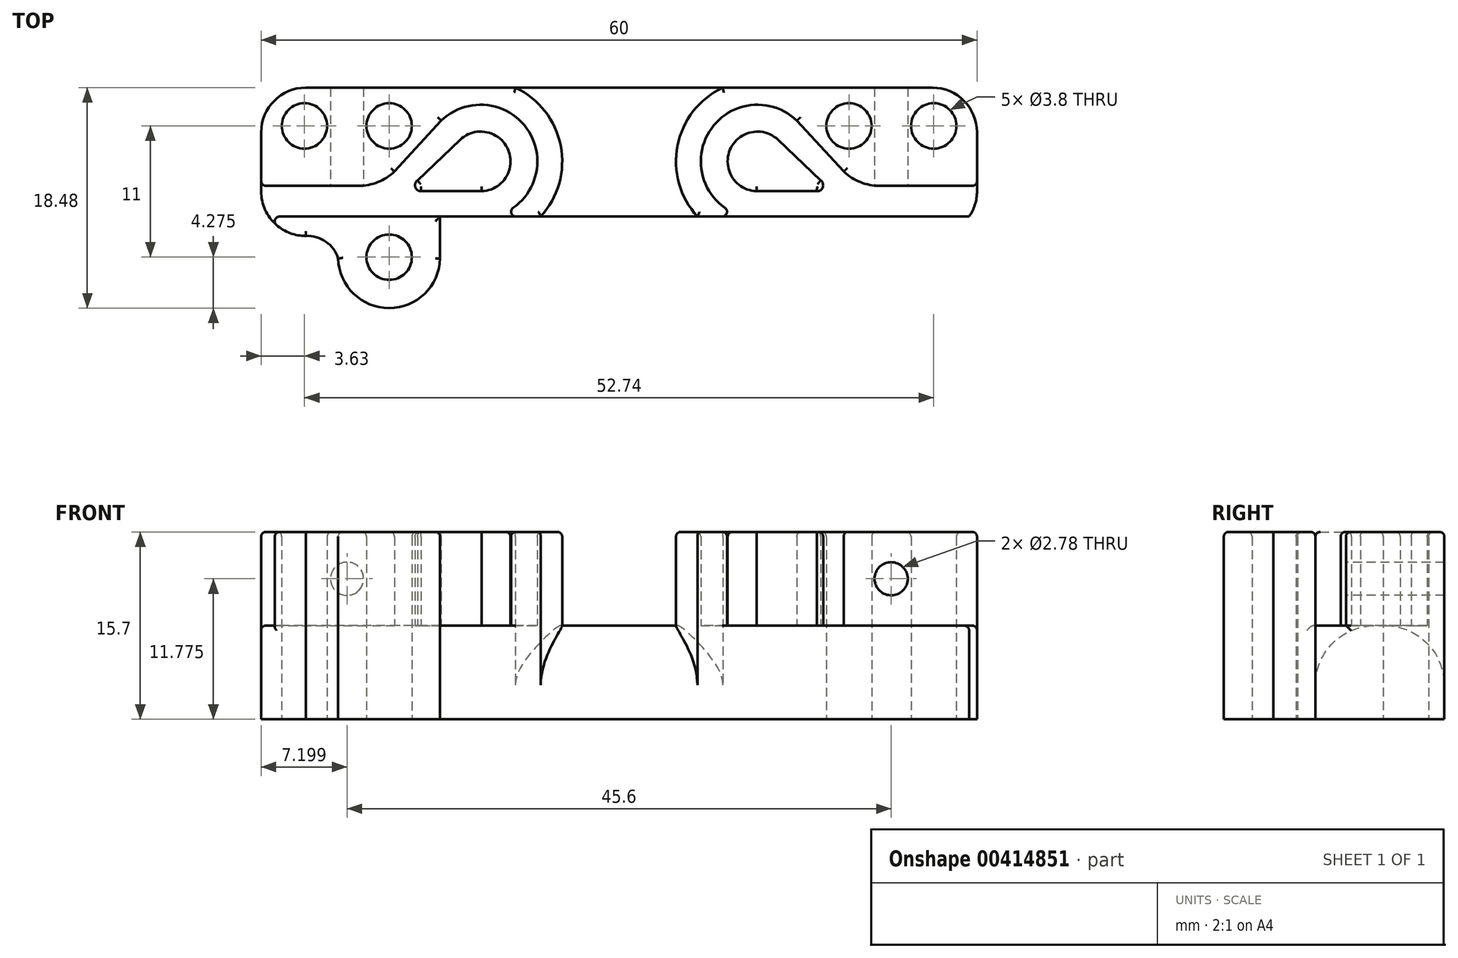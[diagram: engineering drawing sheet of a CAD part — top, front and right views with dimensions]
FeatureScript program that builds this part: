
annotation { "Feature Type Name" : "Feature", "Feature Type Description" : "" }
export const myFeature = defineFeature(function(context is Context, id is Id, definition is map)
    precondition{}
    {
        {
            var Q0;
            Q0=qCreatedBy(makeId("Top.planeOp"),FACE);
            cPlane(context, id + "F0", {"entities" : qUnion([Q0]), "cplaneType" : CPlaneType.OFFSET, "offset" : 7.85 * mm, "oppositeDirection" : true, "width" : 150 * mm, "height" : 150 * mm});
        }
        {
            var Q0;
            Q0=qCreatedBy(id+"F0.planeOp",FACE);
            var sketch = newSketch(context, id + "F1", { "sketchPlane" : qUnion([Q0])});
            skLineSegment(sketch, "E0.left", {"start": v(-30, 9) * mm, "end": v(-30, -9) * mm, "construction": true});
            skLineSegment(sketch, "E0.right", {"start": v(30, 9) * mm, "end": v(30, -9) * mm, "construction": true});
            skPoint(sketch, "E0.middle", {"position": v(0, 0) * mm});
            skLineSegment(sketch, "E1", {"start": v(0, 10.81) * mm, "end": v(0, -11.68) * mm, "construction": true});
            skCircle(sketch, "E2", {"center": v(-16.6, 0.82) * mm, "radius": 0.5 * mm, "construction": true});
            skLineSegment(sketch, "E3", {"start": v(-16.9, 1.23) * mm, "end": v(-13.32, 4.63) * mm});
            skLineSegment(sketch, "E4", {"start": v(-16.59, 0.32) * mm, "end": v(-11.53, 0.32) * mm});
            skArc(sketch, "E5", {"start": v(-13.32, 4.63) * mm, "mid": v(-9.3, 3.78) * mm, "end": v(-11.53, 0.32) * mm});
            skArc(sketch, "E6", {"start": v(-16.9, 1.23) * mm, "mid": v(-17.08, 0.66) * mm, "end": v(-16.59, 0.32) * mm});
            skLineSegment(sketch, "E7", {"start": v(-14.9, 6.23) * mm, "end": v(-18.83, 1.97) * mm});
            skLineSegment(sketch, "E8", {"start": v(-30, 0.77) * mm, "end": v(-21.86, 0.77) * mm});
            skArc(sketch, "E9", {"start": v(-21.86, 0.77) * mm, "mid": v(-20.23, 1.08) * mm, "end": v(-18.83, 1.97) * mm});
            skArc(sketch, "E10", {"start": v(-10.5, -1.8) * mm, "mid": v(-7.44, 5.1) * mm, "end": v(-14.9, 6.23) * mm});
            skCircle(sketch, "E11", {"center": v(-19.27, -5.2) * mm, "radius": 1.9 * mm});
            skCircle(sketch, "E12", {"center": v(-19.27, 5.8) * mm, "radius": 1.9 * mm});
            skCircle(sketch, "E13", {"center": v(-26.37, 5.8) * mm, "radius": 1.9 * mm});
            skLineSegment(sketch, "E14", {"start": v(-15, -1.8) * mm, "end": v(-15, -5.32) * mm});
            skArc(sketch, "E15", {"start": v(-15, -5.32) * mm, "mid": v(-19.27, -9.48) * mm, "end": v(-23.54, -5.32) * mm});
            skArc(sketch, "E16", {"start": v(-30, 5.25) * mm, "mid": v(-28.9, 7.9) * mm, "end": v(-26.25, 9) * mm});
            skArc(sketch, "E17.MirrorCS", {"start": v(-30, 0.32) * mm, "mid": v(-28.9, -2.33) * mm, "end": v(-26.25, -3.43) * mm});
            skLineSegment(sketch, "E18", {"start": v(-30, 5.25) * mm, "end": v(-30, 0.32) * mm});
            skArc(sketch, "E19", {"start": v(-23.54, -5.32) * mm, "mid": v(-24.57, -3.91) * mm, "end": v(-26.25, -3.43) * mm});
            skLineSegment(sketch, "E20", {"start": v(-10.5, -1.8) * mm, "end": v(-29.34, -1.8) * mm});
            skArc(sketch, "E21.MirrorCS", {"start": v(30, 5.25) * mm, "mid": v(28.9, 7.9) * mm, "end": v(26.25, 9) * mm});
            skLineSegment(sketch, "E22.MirrorCS", {"start": v(30, 5.25) * mm, "end": v(30, 0.32) * mm});
            skArc(sketch, "E23.MirrorCS", {"start": v(30, 0.32) * mm, "mid": v(28.9, -2.33) * mm, "end": v(26.25, -3.43) * mm});
            skArc(sketch, "E24.MirrorCS", {"start": v(23.54, -5.32) * mm, "mid": v(24.57, -3.91) * mm, "end": v(26.25, -3.43) * mm});
            skArc(sketch, "E25.MirrorCS", {"start": v(15, -5.32) * mm, "mid": v(19.27, -9.48) * mm, "end": v(23.54, -5.32) * mm});
            skLineSegment(sketch, "E26.MirrorCS", {"start": v(15, -1.8) * mm, "end": v(15, -5.32) * mm});
            skLineSegment(sketch, "E27.MirrorCS", {"start": v(10.5, -1.8) * mm, "end": v(29.34, -1.8) * mm});
            skLineSegment(sketch, "E28.MirrorCS", {"start": v(14.9, 6.23) * mm, "end": v(18.83, 1.97) * mm});
            skArc(sketch, "E29.MirrorCS", {"start": v(21.86, 0.77) * mm, "mid": v(20.23, 1.08) * mm, "end": v(18.83, 1.97) * mm});
            skLineSegment(sketch, "E30.MirrorCS", {"start": v(30, 0.77) * mm, "end": v(21.86, 0.77) * mm});
            skCircle(sketch, "E31.MirrorC", {"center": v(19.27, -5.2) * mm, "radius": 1.9 * mm});
            skCircle(sketch, "E32.MirrorC", {"center": v(19.27, 5.8) * mm, "radius": 1.9 * mm});
            skCircle(sketch, "E33.MirrorC", {"center": v(26.37, 5.8) * mm, "radius": 1.9 * mm});
            skArc(sketch, "E34.MirrorCS", {"start": v(10.5, -1.8) * mm, "mid": v(7.44, 5.1) * mm, "end": v(14.9, 6.23) * mm});
            skLineSegment(sketch, "E35.MirrorCS", {"start": v(16.9, 1.23) * mm, "end": v(13.32, 4.63) * mm});
            skArc(sketch, "E36.MirrorCS", {"start": v(13.32, 4.63) * mm, "mid": v(9.3, 3.78) * mm, "end": v(11.53, 0.32) * mm});
            skLineSegment(sketch, "E37.MirrorCS", {"start": v(16.59, 0.32) * mm, "end": v(11.53, 0.32) * mm});
            skArc(sketch, "E38.MirrorCS", {"start": v(16.9, 1.23) * mm, "mid": v(17.08, 0.66) * mm, "end": v(16.59, 0.32) * mm});
            skLineSegment(sketch, "E39", {"start": v(-26.25, 9) * mm, "end": v(26.25, 9) * mm});
            skLineSegment(sketch, "E40", {"start": v(10.5, -1.8) * mm, "end": v(-10.5, -1.8) * mm});
            skSolve(sketch);
        }
        {
            var Q0;
            Q0=qCreatedBy(makeId("Top.planeOp"),FACE);
            var sketch = newSketch(context, id + "F2", { "sketchPlane" : qUnion([Q0])});
            skLineSegment(sketch, "E41.left", {"start": v(-30, 9) * mm, "end": v(-30, -9) * mm, "construction": true});
            skLineSegment(sketch, "E41.right", {"start": v(30, 9) * mm, "end": v(30, -9) * mm, "construction": true});
            skPoint(sketch, "E41.middle", {"position": v(0, 0) * mm});
            skLineSegment(sketch, "E42", {"start": v(0, 10.81) * mm, "end": v(0, -11.68) * mm, "construction": true});
            skCircle(sketch, "E43", {"center": v(-16.6, 0.82) * mm, "radius": 0.5 * mm, "construction": true});
            skLineSegment(sketch, "E44", {"start": v(-16.9, 1.23) * mm, "end": v(-13.32, 4.63) * mm});
            skLineSegment(sketch, "E45", {"start": v(-16.59, 0.32) * mm, "end": v(-11.53, 0.32) * mm});
            skArc(sketch, "E46", {"start": v(-13.32, 4.63) * mm, "mid": v(-9.3, 3.78) * mm, "end": v(-11.53, 0.32) * mm});
            skArc(sketch, "E47", {"start": v(-16.9, 1.23) * mm, "mid": v(-17.08, 0.66) * mm, "end": v(-16.59, 0.32) * mm});
            skLineSegment(sketch, "E48", {"start": v(-14.9, 6.23) * mm, "end": v(-18.83, 1.97) * mm});
            skLineSegment(sketch, "E49", {"start": v(-30, 0.77) * mm, "end": v(-21.86, 0.77) * mm});
            skArc(sketch, "E50", {"start": v(-21.86, 0.77) * mm, "mid": v(-20.23, 1.08) * mm, "end": v(-18.83, 1.97) * mm});
            skArc(sketch, "E51", {"start": v(-10.5, -1.8) * mm, "mid": v(-7.44, 5.1) * mm, "end": v(-14.9, 6.23) * mm});
            skCircle(sketch, "E52", {"center": v(-19.27, -5.2) * mm, "radius": 1.9 * mm});
            skCircle(sketch, "E53", {"center": v(-19.27, 5.8) * mm, "radius": 1.9 * mm});
            skCircle(sketch, "E54", {"center": v(-26.37, 5.8) * mm, "radius": 1.9 * mm});
            skLineSegment(sketch, "E55", {"start": v(-15, -1.8) * mm, "end": v(-15, -5.32) * mm});
            skArc(sketch, "E56", {"start": v(-15, -5.32) * mm, "mid": v(-19.27, -9.48) * mm, "end": v(-23.54, -5.32) * mm});
            skArc(sketch, "E57", {"start": v(-30, 5.25) * mm, "mid": v(-28.9, 7.9) * mm, "end": v(-26.25, 9) * mm});
            skArc(sketch, "E58.MirrorCS", {"start": v(-30, 0.32) * mm, "mid": v(-28.9, -2.33) * mm, "end": v(-26.25, -3.43) * mm});
            skLineSegment(sketch, "E59", {"start": v(-30, 5.25) * mm, "end": v(-30, 0.32) * mm});
            skArc(sketch, "E60", {"start": v(-23.54, -5.32) * mm, "mid": v(-24.57, -3.91) * mm, "end": v(-26.25, -3.43) * mm});
            skLineSegment(sketch, "E61", {"start": v(-10.5, -1.8) * mm, "end": v(-29.34, -1.8) * mm});
            skArc(sketch, "E62.MirrorCS", {"start": v(30, 5.25) * mm, "mid": v(28.9, 7.9) * mm, "end": v(26.25, 9) * mm});
            skLineSegment(sketch, "E63.MirrorCS", {"start": v(30, 5.25) * mm, "end": v(30, 0.32) * mm});
            skArc(sketch, "E64.MirrorCS", {"start": v(30, 0.32) * mm, "mid": v(28.9, -2.33) * mm, "end": v(26.25, -3.43) * mm});
            skArc(sketch, "E65.MirrorCS", {"start": v(23.54, -5.32) * mm, "mid": v(24.57, -3.91) * mm, "end": v(26.25, -3.43) * mm});
            skArc(sketch, "E66.MirrorCS", {"start": v(15, -5.32) * mm, "mid": v(19.27, -9.48) * mm, "end": v(23.54, -5.32) * mm});
            skLineSegment(sketch, "E67.MirrorCS", {"start": v(15, -1.8) * mm, "end": v(15, -5.32) * mm});
            skLineSegment(sketch, "E68.MirrorCS", {"start": v(10.5, -1.8) * mm, "end": v(29.34, -1.8) * mm});
            skLineSegment(sketch, "E69.MirrorCS", {"start": v(14.9, 6.23) * mm, "end": v(18.83, 1.97) * mm});
            skArc(sketch, "E70.MirrorCS", {"start": v(21.86, 0.77) * mm, "mid": v(20.23, 1.08) * mm, "end": v(18.83, 1.97) * mm});
            skLineSegment(sketch, "E71.MirrorCS", {"start": v(30, 0.77) * mm, "end": v(21.86, 0.77) * mm});
            skCircle(sketch, "E72.MirrorC", {"center": v(19.27, -5.2) * mm, "radius": 1.9 * mm});
            skCircle(sketch, "E73.MirrorC", {"center": v(19.27, 5.8) * mm, "radius": 1.9 * mm});
            skCircle(sketch, "E74.MirrorC", {"center": v(26.37, 5.8) * mm, "radius": 1.9 * mm});
            skArc(sketch, "E75.MirrorCS", {"start": v(10.5, -1.8) * mm, "mid": v(7.44, 5.1) * mm, "end": v(14.9, 6.23) * mm});
            skLineSegment(sketch, "E76.MirrorCS", {"start": v(16.9, 1.23) * mm, "end": v(13.32, 4.63) * mm});
            skArc(sketch, "E77.MirrorCS", {"start": v(13.32, 4.63) * mm, "mid": v(9.3, 3.78) * mm, "end": v(11.53, 0.32) * mm});
            skLineSegment(sketch, "E78.MirrorCS", {"start": v(16.59, 0.32) * mm, "end": v(11.53, 0.32) * mm});
            skArc(sketch, "E79.MirrorCS", {"start": v(16.9, 1.23) * mm, "mid": v(17.08, 0.66) * mm, "end": v(16.59, 0.32) * mm});
            skLineSegment(sketch, "E80", {"start": v(-26.25, 9) * mm, "end": v(26.25, 9) * mm});
            skLineSegment(sketch, "E81", {"start": v(10.5, -1.8) * mm, "end": v(-10.5, -1.8) * mm});
            skCircle(sketch, "E82", {"center": v(0, 0) * mm, "radius": 0.5 * mm, "construction": true});
            skArc(sketch, "E83", {"start": v(-8.69, 9) * mm, "mid": v(-4.9, 4.14) * mm, "end": v(-6.57, -1.8) * mm});
            skArc(sketch, "E84.MirrorCS", {"start": v(8.69, 9) * mm, "mid": v(4.9, 4.14) * mm, "end": v(6.57, -1.8) * mm});
            skSolve(sketch);
        }
        {
            var Q0;
            Q0=qCreatedBy(makeId("Front.planeOp"),FACE);
            var sketch = newSketch(context, id + "F3", { "sketchPlane" : qUnion([Q0])});
            skLineSegment(sketch, "E85.bottom", {"start": v(30, -7.85) * mm, "end": v(-30, -7.85) * mm, "construction": true});
            skLineSegment(sketch, "E85.top", {"start": v(30, 7.85) * mm, "end": v(-30, 7.85) * mm, "construction": true});
            skLineSegment(sketch, "E85.left", {"start": v(30, -7.85) * mm, "end": v(30, 7.85) * mm, "construction": true});
            skLineSegment(sketch, "E85.right", {"start": v(-30, -7.85) * mm, "end": v(-30, 7.85) * mm, "construction": true});
            skCircle(sketch, "E86", {"center": v(-22.8, 3.93) * mm, "radius": 1.39 * mm, "construction": true});
            skLineSegment(sketch, "E87", {"start": v(0, 7.85) * mm, "end": v(0, -7.85) * mm, "construction": true});
            skCircle(sketch, "E88.MirrorC", {"center": v(22.8, 3.93) * mm, "radius": 1.39 * mm, "construction": true});
            skSolve(sketch);
        }
        {
            var Q0;
            Q0=makeQuery(id+"F1.imprint","IMPRINT",FACE,{"disambiguationData":[TD([[makeQuery(id+"F1.imprint","IMPRINT",EDGE,{"derivedFrom":sQuery(id+"F1.wireOp",EDGE,"E7")}),-1.0]])]});
            var Q1;
            Q1=makeQuery(id+"F1.imprint","IMPRINT",FACE,{"disambiguationData":[TD([[makeQuery(id+"F1.imprint","IMPRINT",EDGE,{"derivedFrom":sQuery(id+"F1.wireOp",EDGE,"E3")}),1.0]])]});
            var Q2;
            Q2=makeQuery(id+"F1.imprint","IMPRINT",FACE,{"disambiguationData":[TD([[makeQuery(id+"F1.imprint","IMPRINT",EDGE,{"derivedFrom":sQuery(id+"F1.wireOp",EDGE,"E11")}),-1.0]])]});
            var Q3;
            Q3=makeQuery(id+"F1.imprint","IMPRINT",FACE,{"disambiguationData":[TD([[makeQuery(id+"F1.imprint","IMPRINT",EDGE,{"derivedFrom":sQuery(id+"F1.wireOp",EDGE,"E3")}),-1.0]])]});
            var Q4;
            Q4=makeQuery(id+"F1.imprint","IMPRINT",FACE,{"disambiguationData":[TD([[makeQuery(id+"F1.imprint","IMPRINT",EDGE,{"derivedFrom":sQuery(id+"F1.wireOp",EDGE,"E28.MirrorCS")}),-1.0]])]});
            var Q5;
            Q5=makeQuery(id+"F1.imprint","IMPRINT",FACE,{"disambiguationData":[TD([[makeQuery(id+"F1.imprint","IMPRINT",EDGE,{"derivedFrom":sQuery(id+"F1.wireOp",EDGE,"E35.MirrorCS")}),1.0]])]});
            var Q6;
            {var subQ1=sQuery(id+"F1.wireOp",EDGE,"E24.MirrorCS");Q6=makeQuery(id+"F1.imprint","IMPRINT",FACE,{"disambiguationData":[TD([[makeQuery(id+"F1.imprint","IMPRINT",EDGE,{"derivedFrom":subQ1}),1.0]])]});}
            extrude(context, id + "F4", {"entities" : qUnion([Q0, Q1, Q2, Q3, Q4, Q5, Q6]), "depth" : 7.85 * mm});
        }
        {
            var Q0;
            Q0=makeQuery(id+"F2.imprint","IMPRINT",FACE,{"disambiguationData":[TD([[makeQuery(id+"F2.imprint","IMPRINT",EDGE,{"derivedFrom":sQuery(id+"F2.wireOp",EDGE,"E48")}),-1.0]])]});
            var Q1;
            Q1=makeQuery(id+"F2.imprint","IMPRINT",FACE,{"disambiguationData":[TD([[makeQuery(id+"F2.imprint","IMPRINT",EDGE,{"derivedFrom":sQuery(id+"F2.wireOp",EDGE,"E52")}),-1.0]])]});
            var Q2;
            Q2=makeQuery(id+"F2.imprint","IMPRINT",FACE,{"disambiguationData":[TD([[makeQuery(id+"F2.imprint","IMPRINT",EDGE,{"derivedFrom":sQuery(id+"F2.wireOp",EDGE,"E44")}),-1.0]])]});
            var Q3;
            {var subQ1=sQuery(id+"F2.wireOp",EDGE,"E65.MirrorCS");Q3=makeQuery(id+"F2.imprint","IMPRINT",FACE,{"disambiguationData":[TD([[makeQuery(id+"F2.imprint","IMPRINT",EDGE,{"derivedFrom":subQ1}),1.0]])]});}
            var Q4;
            Q4=makeQuery(id+"F2.imprint","IMPRINT",FACE,{"disambiguationData":[TD([[makeQuery(id+"F2.imprint","IMPRINT",EDGE,{"derivedFrom":sQuery(id+"F2.wireOp",EDGE,"E76.MirrorCS")}),1.0]])]});
            var Q5;
            {var subQ4=sQuery(id+"F2.wireOp",EDGE,"E62.MirrorCS");Q5=makeQuery(id+"F2.imprint","IMPRINT",FACE,{"disambiguationData":[TD([[makeQuery(id+"F2.imprint","IMPRINT",EDGE,{"derivedFrom":subQ4}),1.0]])]});}
            extrude(context, id + "F5", {"entities" : qUnion([Q0, Q1, Q2, Q3, Q4, Q5]), "operationType" : NewBodyOperationType.ADD, "depth" : 7.85 * mm});
        }
        {
            var Q0;
            Q0=sQuery(id+"F3.wireOp",VERTEX,"E88.MirrorC.center");
            var Q1;
            Q1=sQuery(id+"F3.wireOp",VERTEX,"E86.center");
            var Q2;
            Q2=makeQuery(id+"F4.opExtrude","SWEPT_BODY",BODY,{"disambiguationData":[OSD([sQuery(id+"F1.wireOp",EDGE,"E11"),sQuery(id+"F1.wireOp",EDGE,"E12"),sQuery(id+"F1.wireOp",EDGE,"E13"),sQuery(id+"F1.wireOp",EDGE,"E14"),sQuery(id+"F1.wireOp",EDGE,"E15"),sQuery(id+"F1.wireOp",EDGE,"E16"),sQuery(id+"F1.wireOp",EDGE,"E17.MirrorCS"),sQuery(id+"F1.wireOp",EDGE,"E18"),sQuery(id+"F1.wireOp",EDGE,"E19"),sQuery(id+"F1.wireOp",EDGE,"E20"),sQuery(id+"F1.wireOp",EDGE,"E21.MirrorCS"),sQuery(id+"F1.wireOp",EDGE,"E22.MirrorCS"),sQuery(id+"F1.wireOp",EDGE,"E23.MirrorCS"),sQuery(id+"F1.wireOp",EDGE,"E24.MirrorCS"),sQuery(id+"F1.wireOp",EDGE,"E25.MirrorCS"),sQuery(id+"F1.wireOp",EDGE,"E26.MirrorCS"),sQuery(id+"F1.wireOp",EDGE,"E27.MirrorCS"),sQuery(id+"F1.wireOp",EDGE,"E31.MirrorC"),sQuery(id+"F1.wireOp",EDGE,"E32.MirrorC"),sQuery(id+"F1.wireOp",EDGE,"E33.MirrorC"),sQuery(id+"F1.wireOp",EDGE,"E39"),sQuery(id+"F1.wireOp",EDGE,"E40")])]});
            hole(context, id + "F6", {"style" : HoleStyle.SIMPLE, "endStyle" : HoleEndStyle.BLIND, "holeDiameter" : 2.78 * mm, "holeDepth" : 10 * mm, "isTappedThrough" : true, "tappedDepth" : 12 * mm, "tapClearance" : 3, "startFromSketch" : true, "locations" : qUnion([Q0, Q1]), "scope" : qUnion([Q2])});
        }
        {
            var Q0;
            Q0=makeQuery(id+"F5.opExtrude","CAP_FACE",FACE,{"disambiguationData":[OSD([sQuery(id+"F2.wireOp",EDGE,"E64.MirrorCS"),sQuery(id+"F2.wireOp",EDGE,"E65.MirrorCS"),sQuery(id+"F2.wireOp",EDGE,"E66.MirrorCS"),sQuery(id+"F2.wireOp",EDGE,"E67.MirrorCS"),sQuery(id+"F2.wireOp",EDGE,"E68.MirrorCS"),sQuery(id+"F2.wireOp",EDGE,"E72.MirrorC")])],"isStart":false});
            var Q1;
            Q1=makeQuery(id+"F5.opExtrude","CAP_FACE",FACE,{"disambiguationData":[OSD([sQuery(id+"F2.wireOp",EDGE,"E52"),sQuery(id+"F2.wireOp",EDGE,"E55"),sQuery(id+"F2.wireOp",EDGE,"E56"),sQuery(id+"F2.wireOp",EDGE,"E58.MirrorCS"),sQuery(id+"F2.wireOp",EDGE,"E60"),sQuery(id+"F2.wireOp",EDGE,"E61")])],"isStart":false});
            var Q2;
            Q2=makeQuery(id+"F5.opExtrude","CAP_FACE",FACE,{"disambiguationData":[OSD([sQuery(id+"F2.wireOp",EDGE,"E62.MirrorCS"),sQuery(id+"F2.wireOp",EDGE,"E63.MirrorCS"),sQuery(id+"F2.wireOp",EDGE,"E69.MirrorCS"),sQuery(id+"F2.wireOp",EDGE,"E70.MirrorCS"),sQuery(id+"F2.wireOp",EDGE,"E71.MirrorCS"),sQuery(id+"F2.wireOp",EDGE,"E73.MirrorC"),sQuery(id+"F2.wireOp",EDGE,"E74.MirrorC"),sQuery(id+"F2.wireOp",EDGE,"E75.MirrorCS"),sQuery(id+"F2.wireOp",EDGE,"E80"),sQuery(id+"F2.wireOp",EDGE,"E81"),sQuery(id+"F2.wireOp",EDGE,"E84.MirrorCS")])],"isStart":false});
            var Q3;
            Q3=makeQuery(id+"F5.opExtrude","CAP_FACE",FACE,{"disambiguationData":[OSD([sQuery(id+"F2.wireOp",EDGE,"E48"),sQuery(id+"F2.wireOp",EDGE,"E49"),sQuery(id+"F2.wireOp",EDGE,"E50"),sQuery(id+"F2.wireOp",EDGE,"E51"),sQuery(id+"F2.wireOp",EDGE,"E53"),sQuery(id+"F2.wireOp",EDGE,"E54"),sQuery(id+"F2.wireOp",EDGE,"E57"),sQuery(id+"F2.wireOp",EDGE,"E59"),sQuery(id+"F2.wireOp",EDGE,"E80"),sQuery(id+"F2.wireOp",EDGE,"E81"),sQuery(id+"F2.wireOp",EDGE,"E83")])],"isStart":false});
            var Q4;
            Q4=makeQuery(id+"F5.opExtrude","CAP_FACE",FACE,{"disambiguationData":[OSD([sQuery(id+"F2.wireOp",EDGE,"E44"),sQuery(id+"F2.wireOp",EDGE,"E45"),sQuery(id+"F2.wireOp",EDGE,"E46"),sQuery(id+"F2.wireOp",EDGE,"E47")])],"isStart":false});
            var Q5;
            Q5=makeQuery(id+"F5.opExtrude","CAP_FACE",FACE,{"disambiguationData":[OSD([sQuery(id+"F2.wireOp",EDGE,"E76.MirrorCS"),sQuery(id+"F2.wireOp",EDGE,"E77.MirrorCS"),sQuery(id+"F2.wireOp",EDGE,"E78.MirrorCS"),sQuery(id+"F2.wireOp",EDGE,"E79.MirrorCS")])],"isStart":false});
            fillet(context, id + "F7", {"entities" : qUnion([Q0, Q1, Q2, Q3, Q4, Q5]), "radius" : 0.4 * mm, "tangentPropagation" : true, "allowEdgeOverflow" : false});
        }
        {
            var Q0;
            {var subQ2=sQuery(id+"F1.wireOp",EDGE,"E40");var subQ3=sQuery(id+"F1.wireOp",EDGE,"E27.MirrorCS");var subQ4=sQuery(id+"F1.wireOp",EDGE,"E20");var subQ5=sQuery(id+"F2.wireOp",EDGE,"E83");Q0=makeQuery(id+"F5.boolean.opBoolean","SPLIT",EDGE,{"disambiguationData":[TD([makeQuery(id+"F5.opExtrude","SWEPT_FACE",FACE,{"disambiguationData":[OSD([subQ5])]})])],"derivedFrom":makeQuery(id+"F4.opExtrude","CAP_EDGE",EDGE,{"disambiguationData":[OSD([subQ4,subQ3,subQ2])],"isStart":false})});}
            var Q1;
            Q1=makeQuery(id+"F4.opExtrude","CAP_EDGE",EDGE,{"disambiguationData":[OSD([sQuery(id+"F1.wireOp",EDGE,"E39")])],"isStart":false});
            fillet(context, id + "F8", {"entities" : qUnion([Q0, Q1]), "radius" : 5 * mm, "tangentPropagation" : true, "allowEdgeOverflow" : false});
        }
        {
            var Q0;
            Q0=makeQuery(id+"F5.opExtrude","SWEPT_EDGE",EDGE,{"disambiguationData":[OSD([sQuery(id+"F2.wireOp",EDGE,"E64.MirrorCS"),sQuery(id+"F2.wireOp",EDGE,"E68.MirrorCS")])]});
            var Q1;
            Q1=makeQuery(id+"F5.opExtrude","SWEPT_EDGE",EDGE,{"disambiguationData":[OSD([sQuery(id+"F2.wireOp",EDGE,"E63.MirrorCS"),sQuery(id+"F2.wireOp",EDGE,"E71.MirrorCS")])]});
            var Q2;
            Q2=makeQuery(id+"F4.opExtrude","CAP_EDGE",EDGE,{"disambiguationData":[OSD([sQuery(id+"F1.wireOp",EDGE,"E23.MirrorCS")])],"isStart":false});
            var Q3;
            Q3=makeQuery(id+"F5.opExtrude","SWEPT_EDGE",EDGE,{"disambiguationData":[OSD([sQuery(id+"F2.wireOp",EDGE,"E58.MirrorCS"),sQuery(id+"F2.wireOp",EDGE,"E61")])]});
            var Q4;
            Q4=makeQuery(id+"F4.opExtrude","CAP_EDGE",EDGE,{"disambiguationData":[OSD([sQuery(id+"F1.wireOp",EDGE,"E17.MirrorCS")])],"isStart":false});
            var Q5;
            Q5=makeQuery(id+"F5.opExtrude","SWEPT_EDGE",EDGE,{"disambiguationData":[OSD([sQuery(id+"F2.wireOp",EDGE,"E49"),sQuery(id+"F2.wireOp",EDGE,"E59")])]});
            var Q6;
            Q6=makeQuery(id+"F5.opExtrude","SWEPT_EDGE",EDGE,{"disambiguationData":[OSD([sQuery(id+"F2.wireOp",EDGE,"E68.MirrorCS"),sQuery(id+"F2.wireOp",EDGE,"E75.MirrorCS"),sQuery(id+"F2.wireOp",EDGE,"E81")])]});
            var Q7;
            Q7=makeQuery(id+"F5.opExtrude","SWEPT_EDGE",EDGE,{"disambiguationData":[OSD([sQuery(id+"F2.wireOp",EDGE,"E51"),sQuery(id+"F2.wireOp",EDGE,"E61"),sQuery(id+"F2.wireOp",EDGE,"E81")])]});
            var Q8;
            {var subQ0=sQuery(id+"F2.wireOp",EDGE,"E80");Q8=makeQuery(id+"F6.hole-0.boolean.opBoolean","INTERSECT",EDGE,{"derivedFrom":[makeQuery(id+"F5.boolean.opBoolean","MERGE",FACE,{"derivedFrom":[makeQuery(id+"F4.opExtrude","SWEPT_FACE",FACE,{"disambiguationData":[OSD([sQuery(id+"F1.wireOp",EDGE,"E39")])]}),makeQuery(id+"F5.opExtrude","SWEPT_FACE",FACE,{"disambiguationData":[OSD([subQ0]),TDD([makeQuery(id+"F2.imprint","IMPRINT",EDGE,{"disambiguationData":[TD([[makeQuery(id+"F2.imprint","INTERSECT",VERTEX,{"derivedFrom":[sQuery(id+"F2.wireOp",EDGE,"E57"),subQ0]}),-1.0]])],"derivedFrom":subQ0})])]}),makeQuery(id+"F5.opExtrude","SWEPT_FACE",FACE,{"disambiguationData":[OSD([subQ0]),TDD([makeQuery(id+"F2.imprint","IMPRINT",EDGE,{"disambiguationData":[TD([[makeQuery(id+"F2.imprint","INTERSECT",VERTEX,{"derivedFrom":[sQuery(id+"F2.wireOp",EDGE,"E62.MirrorCS"),subQ0]}),1.0]])],"derivedFrom":subQ0})])]})]}),makeQuery(id+"F6.hole-0.opRevolve","SWEPT_FACE",FACE,{"disambiguationData":[OSD([sQuery(id+"F6.hole-0.sketch.wireOp",EDGE,"core_line_2")])]})]});}
            var Q9;
            {var subQ0=sQuery(id+"F2.wireOp",EDGE,"E80");Q9=makeQuery(id+"F6.hole-1.boolean.opBoolean","INTERSECT",EDGE,{"derivedFrom":[makeQuery(id+"F5.boolean.opBoolean","MERGE",FACE,{"derivedFrom":[makeQuery(id+"F4.opExtrude","SWEPT_FACE",FACE,{"disambiguationData":[OSD([sQuery(id+"F1.wireOp",EDGE,"E39")])]}),makeQuery(id+"F5.opExtrude","SWEPT_FACE",FACE,{"disambiguationData":[OSD([subQ0]),TDD([makeQuery(id+"F2.imprint","IMPRINT",EDGE,{"disambiguationData":[TD([[makeQuery(id+"F2.imprint","INTERSECT",VERTEX,{"derivedFrom":[sQuery(id+"F2.wireOp",EDGE,"E57"),subQ0]}),-1.0]])],"derivedFrom":subQ0})])]}),makeQuery(id+"F5.opExtrude","SWEPT_FACE",FACE,{"disambiguationData":[OSD([subQ0]),TDD([makeQuery(id+"F2.imprint","IMPRINT",EDGE,{"disambiguationData":[TD([[makeQuery(id+"F2.imprint","INTERSECT",VERTEX,{"derivedFrom":[sQuery(id+"F2.wireOp",EDGE,"E62.MirrorCS"),subQ0]}),1.0]])],"derivedFrom":subQ0})])]})]}),makeQuery(id+"F6.hole-1.opRevolve","SWEPT_FACE",FACE,{"disambiguationData":[OSD([sQuery(id+"F6.hole-1.sketch.wireOp",EDGE,"core_line_2")])]})]});}
            fillet(context, id + "F9", {"entities" : qUnion([Q0, Q1, Q2, Q3, Q4, Q5, Q6, Q7, Q8, Q9]), "radius" : 0.4 * mm, "tangentPropagation" : true, "allowEdgeOverflow" : false});
        }
    });
